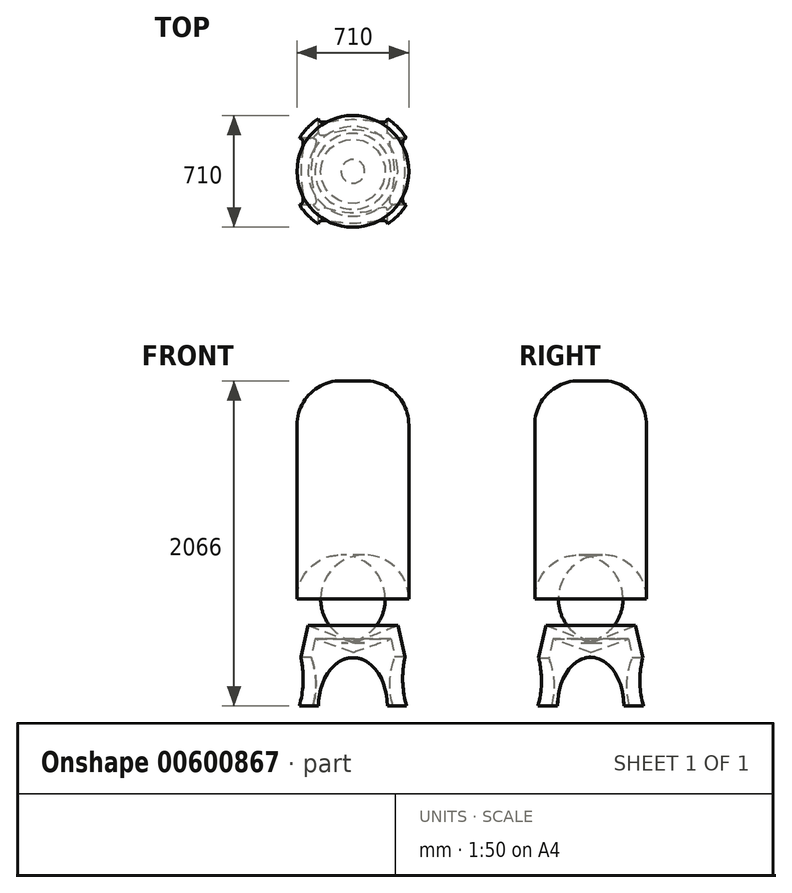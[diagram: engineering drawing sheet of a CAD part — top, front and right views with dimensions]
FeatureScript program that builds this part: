
annotation { "Feature Type Name" : "Feature", "Feature Type Description" : "" }
export const myFeature = defineFeature(function(context is Context, id is Id, definition is map)
    precondition{}
    {
        {
            var Q0;
            Q0=qCreatedBy(makeId("Front.planeOp"),FACE);
            var sketch = newSketch(context, id + "F0", { "sketchPlane" : qUnion([Q0])});
            skLineSegment(sketch, "E0", {"start": v(0, 0) * mm, "end": v(0, 1666) * mm});
            skLineSegment(sketch, "E1.bottom", {"start": v(0, 1666) * mm, "end": v(75, 1666) * mm});
            skLineSegment(sketch, "E1.top", {"start": v(0, 0) * mm, "end": v(75, 0) * mm});
            skLineSegment(sketch, "E1.left", {"start": v(0, 1666) * mm, "end": v(0, 0) * mm});
            skLineSegment(sketch, "E1.right", {"start": v(355, 1386) * mm, "end": v(355, 280) * mm});
            skPoint(sketch, "E2.visualSharp", {"position": v(355, 1666) * mm});
            skArc(sketch, "E2.filletArc", {"start": v(355, 1386) * mm, "mid": v(272.99, 1583.99) * mm, "end": v(75, 1666) * mm});
            skPoint(sketch, "E3.visualSharp", {"position": v(355, 0) * mm});
            skArc(sketch, "E3.filletArc", {"start": v(75, 0) * mm, "mid": v(272.99, 82.01) * mm, "end": v(355, 280) * mm});
            skSolve(sketch);
        }
        {
            var Q0;
            Q0=makeQuery(id+"F0.imprint","IMPRINT",FACE,{"disambiguationData":[TD([[makeQuery(id+"F0.imprint","IMPRINT",EDGE,{"derivedFrom":sQuery(id+"F0.wireOp",EDGE,"E1.bottom")}),-1.0]])]});
            var Q1;
            Q1=sQuery(id+"F0.wireOp",EDGE,"E1.left");
            revolve(context, id + "F1", {"entities" : qUnion([Q0]), "axis" : qUnion([Q1]), "revolveType" : RevolveType.FULL});
        }
        {
            var Q0;
            Q0=qCreatedBy(makeId("Front.planeOp"),FACE);
            var sketch = newSketch(context, id + "F2", { "sketchPlane" : qUnion([Q0])});
            skLineSegment(sketch, "E4", {"start": v(0, 0) * mm, "end": v(0, -58.67) * mm});
            skLineSegment(sketch, "E5", {"start": v(330.12, -400) * mm, "end": v(400, -400) * mm});
            skLineSegment(sketch, "E6", {"start": v(400, -400) * mm, "end": v(284.77, 112.64) * mm});
            skLineSegment(sketch, "E7", {"start": v(284.77, 112.64) * mm, "end": v(0, 0) * mm});
            skLineSegment(sketch, "E8", {"start": v(330.12, -400) * mm, "end": v(240.95, 25.55) * mm});
            skLineSegment(sketch, "E9", {"start": v(240.95, 25.55) * mm, "end": v(0, -58.67) * mm});
            skSolve(sketch);
        }
        {
            var Q0;
            Q0=makeQuery(id+"F2.imprint","IMPRINT",FACE,{"disambiguationData":[TD([[makeQuery(id+"F2.imprint","IMPRINT",EDGE,{"derivedFrom":sQuery(id+"F2.wireOp",EDGE,"E4")}),1.0]])]});
            var Q1;
            Q1=sQuery(id+"F2.wireOp",EDGE,"E4");
            revolve(context, id + "F3", {"entities" : qUnion([Q0]), "axis" : qUnion([Q1]), "revolveType" : RevolveType.FULL});
        }
        {
            var Q0;
            Q0=qCreatedBy(makeId("Front.planeOp"),FACE);
            var sketch = newSketch(context, id + "F4", { "sketchPlane" : qUnion([Q0])});
            skEllipse(sketch, "E10", {"center": v(0, -400.04) * mm, "majorRadius": 307.15 * mm, "minorRadius": 218.7 * mm, "majorAxis": v(0, -1)});
            skSolve(sketch);
        }
        {
            var Q0;
            Q0=makeQuery(id+"F4.imprint","IMPRINT",FACE,{"disambiguationData":[TD([[makeQuery(id+"F4.imprint","IMPRINT",EDGE,{"derivedFrom":sQuery(id+"F4.wireOp",EDGE,"E10")}),1.0]])]});
            extrude(context, id + "F5", {"entities" : qUnion([Q0]), "operationType" : NewBodyOperationType.REMOVE, "endBound" : BoundingType.SYMMETRIC, "depth" : 800 * mm, "offsetDistance" : 25 * mm});
        }
        {
            var Q0;
            Q0=qCreatedBy(makeId("Right.planeOp"),FACE);
            var sketch = newSketch(context, id + "F6", { "sketchPlane" : qUnion([Q0])});
            skEllipse(sketch, "E11", {"center": v(0, -399.88) * mm, "majorRadius": 310.4 * mm, "minorRadius": 210.53 * mm, "majorAxis": v(0, 1)});
            skSolve(sketch);
        }
        {
            var Q0;
            Q0=makeQuery(id+"F6.imprint","IMPRINT",FACE,{"disambiguationData":[TD([[makeQuery(id+"F6.imprint","IMPRINT",EDGE,{"derivedFrom":sQuery(id+"F6.wireOp",EDGE,"E11")}),1.0]])]});
            extrude(context, id + "F7", {"entities" : qUnion([Q0]), "operationType" : NewBodyOperationType.REMOVE, "endBound" : BoundingType.SYMMETRIC, "oppositeDirection" : true, "depth" : 800 * mm, "offsetDistance" : 25 * mm});
        }
    });
